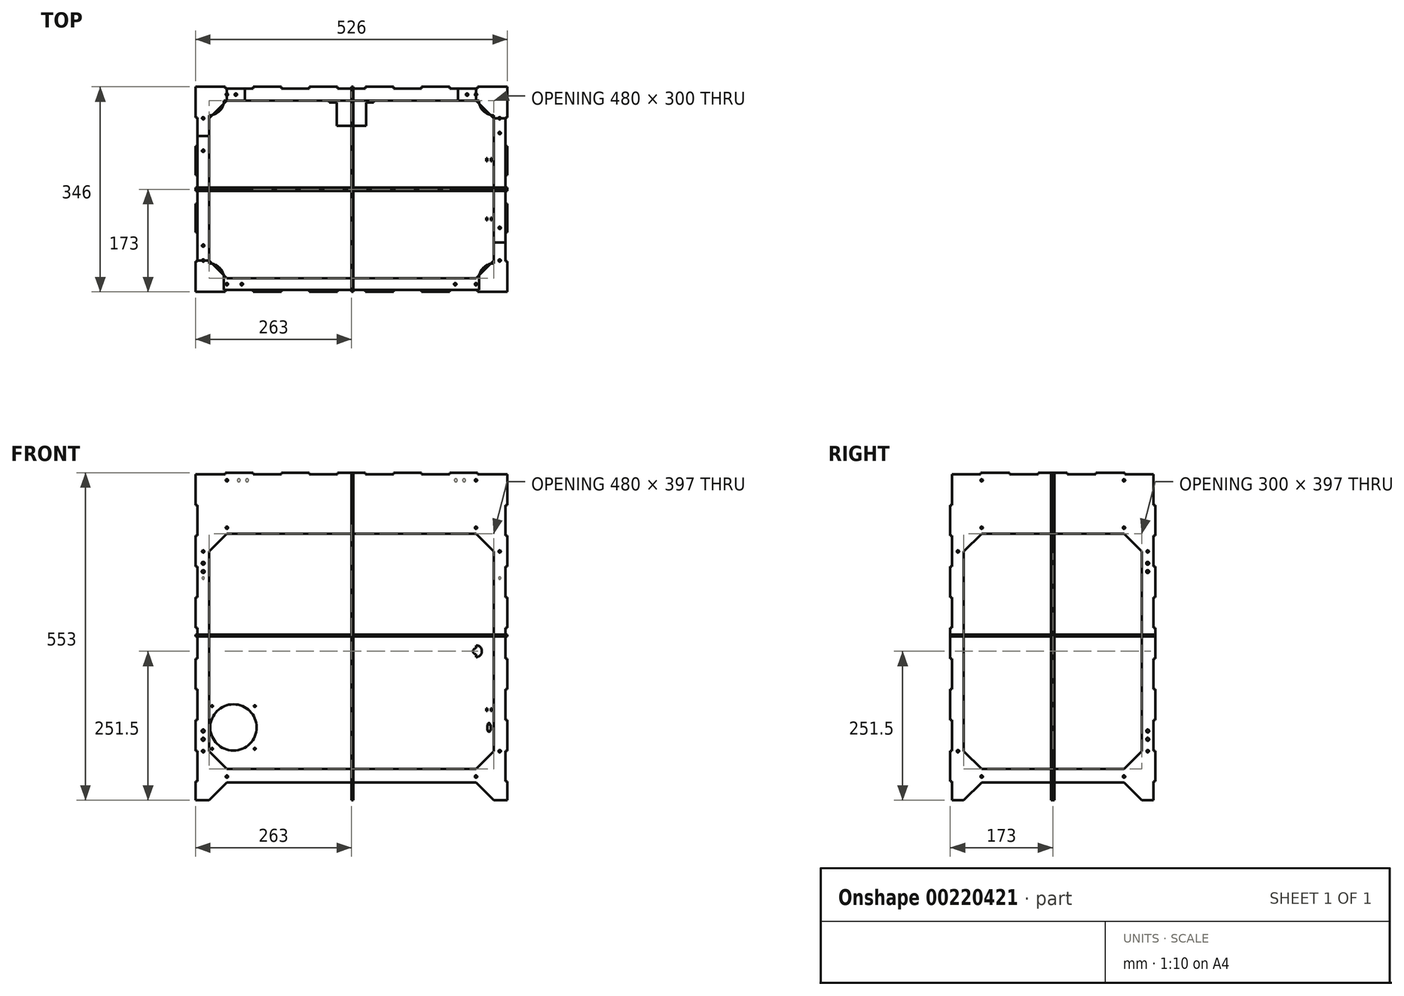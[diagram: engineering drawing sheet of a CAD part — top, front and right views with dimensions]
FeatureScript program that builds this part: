
annotation { "Feature Type Name" : "Feature", "Feature Type Description" : "" }
export const myFeature = defineFeature(function(context is Context, id is Id, definition is map)
    precondition{}
    {
        {
            assignVariable(context, id + "F0", {"name" : "thick", "anyValue" : 3});
        }
        {
            var Q0;
            Q0=qCreatedBy(makeId("Top.planeOp"),FACE);
            var sketch = newSketch(context, id + "F1", { "sketchPlane" : qUnion([Q0])});
            skLineSegment(sketch, "E0.bottom", {"start": v(263, -173) * mm, "end": v(-263, -173) * mm});
            skLineSegment(sketch, "E0.top", {"start": v(263, 173) * mm, "end": v(-263, 173) * mm});
            skLineSegment(sketch, "E0.left", {"start": v(263, -173) * mm, "end": v(263, 173) * mm});
            skLineSegment(sketch, "E0.right", {"start": v(-263, -173) * mm, "end": v(-263, 173) * mm});
            skPoint(sketch, "E0.middle", {"position": v(0, 0) * mm});
            skLineSegment(sketch, "E1.bottom", {"start": v(210, -150) * mm, "end": v(-210, -150) * mm});
            skLineSegment(sketch, "E1.top", {"start": v(210, 150) * mm, "end": v(-210, 150) * mm});
            skLineSegment(sketch, "E1.left", {"start": v(240, -120) * mm, "end": v(240, 120) * mm});
            skLineSegment(sketch, "E1.right", {"start": v(-240, -120) * mm, "end": v(-240, 120) * mm});
            skLineSegment(sketch, "E2", {"start": v(-210, 150) * mm, "end": v(-240, 120) * mm});
            skLineSegment(sketch, "E3", {"start": v(-240, -120) * mm, "end": v(-210, -150) * mm});
            skLineSegment(sketch, "E4", {"start": v(240, -120) * mm, "end": v(210, -150) * mm});
            skLineSegment(sketch, "E5", {"start": v(240, 120) * mm, "end": v(210, 150) * mm});
            skPoint(sketch, "E6.orphan", {"position": v(-240, 150) * mm});
            skPoint(sketch, "E7.orphan", {"position": v(-240, -150) * mm});
            skPoint(sketch, "E8.orphan", {"position": v(240, -150) * mm});
            skPoint(sketch, "E9.orphan", {"position": v(240, 150) * mm});
            skCircle(sketch, "E10", {"center": v(-210, 160) * mm, "radius": 2 * mm});
            skCircle(sketch, "E11", {"center": v(210, 160) * mm, "radius": 2 * mm});
            skCircle(sketch, "E12", {"center": v(-250, 120) * mm, "radius": 2 * mm});
            skCircle(sketch, "E13", {"center": v(-250, -120) * mm, "radius": 2 * mm});
            skCircle(sketch, "E14", {"center": v(-210, -160) * mm, "radius": 2 * mm});
            skCircle(sketch, "E15", {"center": v(210, -160) * mm, "radius": 2 * mm});
            skCircle(sketch, "E16", {"center": v(250, -120) * mm, "radius": 2 * mm});
            skCircle(sketch, "E17", {"center": v(250, 120) * mm, "radius": 2 * mm});
            skLineSegment(sketch, "E18", {"start": v(-212.73, -173) * mm, "end": v(-212.73, -170) * mm});
            skLineSegment(sketch, "E19", {"start": v(-212.73, -170) * mm, "end": v(-165.45, -170) * mm});
            skLineSegment(sketch, "E20", {"start": v(-165.45, -170) * mm, "end": v(-165.45, -173) * mm});
            skLineSegment(sketch, "E21.1.0.0", {"start": v(-118.18, -173) * mm, "end": v(-118.18, -170) * mm});
            skLineSegment(sketch, "E21.1.0.1", {"start": v(-118.18, -170) * mm, "end": v(-70.9, -170) * mm});
            skLineSegment(sketch, "E21.1.0.2", {"start": v(-70.9, -170) * mm, "end": v(-70.9, -173) * mm});
            skLineSegment(sketch, "E21.2.0.0", {"start": v(-23.64, -173) * mm, "end": v(-23.64, -170) * mm});
            skLineSegment(sketch, "E21.2.0.1", {"start": v(-23.64, -170) * mm, "end": v(23.64, -170) * mm});
            skLineSegment(sketch, "E21.2.0.2", {"start": v(23.64, -170) * mm, "end": v(23.64, -173) * mm});
            skLineSegment(sketch, "E21.3.0.0", {"start": v(70.9, -173) * mm, "end": v(70.9, -170) * mm});
            skLineSegment(sketch, "E21.3.0.1", {"start": v(70.9, -170) * mm, "end": v(118.18, -170) * mm});
            skLineSegment(sketch, "E21.3.0.2", {"start": v(118.18, -170) * mm, "end": v(118.18, -173) * mm});
            skLineSegment(sketch, "E21.direction1", {"start": v(-212.73, -173) * mm, "end": v(-118.18, -173) * mm, "construction": true});
            skLineSegment(sketch, "E22", {"start": v(-212.73, 173) * mm, "end": v(-212.73, 170) * mm});
            skLineSegment(sketch, "E23", {"start": v(-212.73, 170) * mm, "end": v(-165.45, 170) * mm});
            skLineSegment(sketch, "E24", {"start": v(-165.45, 170) * mm, "end": v(-165.45, 173) * mm});
            skLineSegment(sketch, "E25.1.0.0", {"start": v(-118.18, 173) * mm, "end": v(-118.18, 170) * mm});
            skLineSegment(sketch, "E25.1.0.1", {"start": v(-118.18, 170) * mm, "end": v(-70.9, 170) * mm});
            skLineSegment(sketch, "E25.1.0.2", {"start": v(-70.9, 170) * mm, "end": v(-70.9, 173) * mm});
            skLineSegment(sketch, "E25.2.0.0", {"start": v(-23.64, 173) * mm, "end": v(-23.64, 170) * mm});
            skLineSegment(sketch, "E25.2.0.1", {"start": v(-23.64, 170) * mm, "end": v(23.64, 170) * mm});
            skLineSegment(sketch, "E25.2.0.2", {"start": v(23.64, 170) * mm, "end": v(23.64, 173) * mm});
            skLineSegment(sketch, "E25.3.0.0", {"start": v(70.9, 173) * mm, "end": v(70.9, 170) * mm});
            skLineSegment(sketch, "E25.3.0.1", {"start": v(70.9, 170) * mm, "end": v(118.18, 170) * mm});
            skLineSegment(sketch, "E25.3.0.2", {"start": v(118.18, 170) * mm, "end": v(118.18, 173) * mm});
            skLineSegment(sketch, "E25.direction1", {"start": v(-212.73, 170) * mm, "end": v(-118.18, 170) * mm, "construction": true});
            skLineSegment(sketch, "E26", {"start": v(-263, -72.86) * mm, "end": v(-260, -72.86) * mm});
            skLineSegment(sketch, "E27", {"start": v(-260, -72.86) * mm, "end": v(-260, -121.43) * mm});
            skLineSegment(sketch, "E28", {"start": v(-260, -121.43) * mm, "end": v(-263, -121.43) * mm});
            skLineSegment(sketch, "E29.0.1.0", {"start": v(-263, 24.29) * mm, "end": v(-260, 24.29) * mm});
            skLineSegment(sketch, "E29.0.1.1", {"start": v(-260, 24.29) * mm, "end": v(-260, -24.29) * mm});
            skLineSegment(sketch, "E29.0.1.2", {"start": v(-260, -24.29) * mm, "end": v(-263, -24.29) * mm});
            skLineSegment(sketch, "E29.0.2.0", {"start": v(-263, 121.43) * mm, "end": v(-260, 121.43) * mm});
            skLineSegment(sketch, "E29.0.2.1", {"start": v(-260, 121.43) * mm, "end": v(-260, 72.86) * mm});
            skLineSegment(sketch, "E29.0.2.2", {"start": v(-260, 72.86) * mm, "end": v(-263, 72.86) * mm});
            skLineSegment(sketch, "E29.direction1", {"start": v(-263, -72.86) * mm, "end": v(-188, -72.86) * mm, "construction": true});
            skLineSegment(sketch, "E29.direction2", {"start": v(-263, -72.86) * mm, "end": v(-263, 24.29) * mm, "construction": true});
            skLineSegment(sketch, "E30", {"start": v(263, -121.43) * mm, "end": v(260, -121.43) * mm});
            skLineSegment(sketch, "E31", {"start": v(260, -121.43) * mm, "end": v(260, -72.86) * mm});
            skLineSegment(sketch, "E32", {"start": v(260, -72.86) * mm, "end": v(263, -72.86) * mm});
            skLineSegment(sketch, "E33.0.1.0", {"start": v(260, 24.29) * mm, "end": v(263, 24.29) * mm});
            skLineSegment(sketch, "E33.0.1.1", {"start": v(260, -24.29) * mm, "end": v(260, 24.29) * mm});
            skLineSegment(sketch, "E33.0.1.2", {"start": v(263, -24.29) * mm, "end": v(260, -24.29) * mm});
            skLineSegment(sketch, "E33.0.2.0", {"start": v(260, 121.43) * mm, "end": v(263, 121.43) * mm});
            skLineSegment(sketch, "E33.0.2.1", {"start": v(260, 72.86) * mm, "end": v(260, 121.43) * mm});
            skLineSegment(sketch, "E33.0.2.2", {"start": v(263, 72.86) * mm, "end": v(260, 72.86) * mm});
            skLineSegment(sketch, "E33.direction1", {"start": v(235, -72.86) * mm, "end": v(260, -72.86) * mm, "construction": true});
            skLineSegment(sketch, "E33.direction2", {"start": v(260, -72.86) * mm, "end": v(260, 24.29) * mm, "construction": true});
            skCircle(sketch, "E34", {"center": v(-190, 160) * mm, "radius": 2 * mm, "construction": true});
            skCircle(sketch, "E35", {"center": v(-176, 160) * mm, "radius": 2 * mm, "construction": true});
            skCircle(sketch, "E36", {"center": v(190, 160) * mm, "radius": 2 * mm, "construction": true});
            skCircle(sketch, "E37", {"center": v(176, 160) * mm, "radius": 2 * mm, "construction": true});
            skPoint(sketch, "E38.centerSnap0", {"position": v(-260, 97.14) * mm});
            skLineSegment(sketch, "E39.0.4.0", {"start": v(165.45, -173) * mm, "end": v(165.45, -170) * mm});
            skLineSegment(sketch, "E39.3.4.0", {"start": v(165.45, -170) * mm, "end": v(212.73, -170) * mm});
            skLineSegment(sketch, "E39.6.4.0", {"start": v(212.73, -170) * mm, "end": v(212.73, -173) * mm});
            skLineSegment(sketch, "E40.0.4.0", {"start": v(165.45, 173) * mm, "end": v(165.45, 170) * mm});
            skLineSegment(sketch, "E40.3.4.0", {"start": v(165.45, 170) * mm, "end": v(212.73, 170) * mm});
            skLineSegment(sketch, "E40.6.4.0", {"start": v(212.73, 170) * mm, "end": v(212.73, 173) * mm});
            skSolve(sketch);
        }
        {
            var Q0;
            Q0=makeQuery(id+"F1.imprint","IMPRINT",FACE,{"disambiguationData":[TD([[makeQuery(id+"F1.imprint","IMPRINT",EDGE,{"derivedFrom":sQuery(id+"F1.wireOp",EDGE,"E0.bottom")}),-1.0]])]});
            extrude(context, id + "F2", {"entities" : qUnion([Q0]), "depth" : (getVariable(context, 'thick')) * mm});
        }
        {
            var Q0;
            Q0=qCreatedBy(makeId("Front.planeOp"),FACE);
            var sketch = newSketch(context, id + "F3", { "sketchPlane" : qUnion([Q0])});
            skLineSegment(sketch, "E41.bottom", {"start": v(263, -276.5) * mm, "end": v(240, -276.5) * mm});
            skLineSegment(sketch, "E41.top", {"start": v(263, 276.5) * mm, "end": v(-263, 276.5) * mm});
            skLineSegment(sketch, "E41.left", {"start": v(263, -276.5) * mm, "end": v(263, 276.5) * mm});
            skLineSegment(sketch, "E41.right", {"start": v(-263, -276.5) * mm, "end": v(-263, 276.5) * mm});
            skPoint(sketch, "E41.middle", {"position": v(0, 0) * mm});
            skLineSegment(sketch, "E42.bottom", {"start": v(210, 173.5) * mm, "end": v(-210, 173.5) * mm});
            skLineSegment(sketch, "E42.top", {"start": v(210, -223.5) * mm, "end": v(-210, -223.5) * mm});
            skLineSegment(sketch, "E42.left", {"start": v(240, 143.5) * mm, "end": v(240, -193.5) * mm});
            skLineSegment(sketch, "E42.right", {"start": v(-240, 143.5) * mm, "end": v(-240, -193.5) * mm});
            skPoint(sketch, "E42.middle", {"position": v(0, -25) * mm});
            skLineSegment(sketch, "E43", {"start": v(-210, 173.5) * mm, "end": v(-240, 143.5) * mm});
            skLineSegment(sketch, "E44", {"start": v(-240, -193.5) * mm, "end": v(-210, -223.5) * mm});
            skLineSegment(sketch, "E45", {"start": v(240, -193.5) * mm, "end": v(210, -223.5) * mm});
            skLineSegment(sketch, "E46", {"start": v(210, 173.5) * mm, "end": v(240, 143.5) * mm});
            skPoint(sketch, "E47.orphan", {"position": v(-240, 173.5) * mm});
            skPoint(sketch, "E48.orphan", {"position": v(-240, -223.5) * mm});
            skPoint(sketch, "E49.orphan", {"position": v(240, 173.5) * mm});
            skPoint(sketch, "E50.orphan", {"position": v(240, -223.5) * mm});
            skLineSegment(sketch, "E51", {"start": v(-240, -276.5) * mm, "end": v(-210, -246.5) * mm});
            skLineSegment(sketch, "E52", {"start": v(-210, -246.5) * mm, "end": v(210, -246.5) * mm});
            skLineSegment(sketch, "E53", {"start": v(210, -246.5) * mm, "end": v(240, -276.5) * mm});
            skLineSegment(sketch, "E54.trimOffspring", {"start": v(-240, -276.5) * mm, "end": v(-263, -276.5) * mm});
            skCircle(sketch, "E55", {"center": v(-210, 263.5) * mm, "radius": 2 * mm});
            skCircle(sketch, "E56", {"center": v(210, 263.5) * mm, "radius": 2 * mm});
            skCircle(sketch, "E57", {"center": v(-210, 183.5) * mm, "radius": 2 * mm});
            skCircle(sketch, "E58", {"center": v(210, 183.5) * mm, "radius": 2 * mm});
            skCircle(sketch, "E59", {"center": v(250, 143.5) * mm, "radius": 2 * mm});
            skCircle(sketch, "E60", {"center": v(-250, 143.5) * mm, "radius": 2 * mm});
            skCircle(sketch, "E61", {"center": v(250, -193.5) * mm, "radius": 2 * mm});
            skCircle(sketch, "E62", {"center": v(210, -236.5) * mm, "radius": 2 * mm});
            skCircle(sketch, "E63", {"center": v(-210, -236.5) * mm, "radius": 2 * mm});
            skCircle(sketch, "E64", {"center": v(-250, -193.5) * mm, "radius": 2 * mm});
            skCircle(sketch, "E65", {"center": v(-250, 123.5) * mm, "radius": 2.5 * mm});
            skCircle(sketch, "E66", {"center": v(-250, 109.5) * mm, "radius": 2.5 * mm});
            skCircle(sketch, "E67", {"center": v(-250, -173.5) * mm, "radius": 2.5 * mm});
            skCircle(sketch, "E68", {"center": v(-250, -159.5) * mm, "radius": 2.5 * mm});
            skLineSegment(sketch, "E69", {"start": v(-260, 276.5) * mm, "end": v(-260, 273.5) * mm});
            skLineSegment(sketch, "E70", {"start": v(-260, 273.5) * mm, "end": v(-212.73, 273.5) * mm});
            skLineSegment(sketch, "E71", {"start": v(-212.73, 273.5) * mm, "end": v(-212.73, 276.5) * mm});
            skLineSegment(sketch, "E72.1.0.0", {"start": v(-165.45, 276.5) * mm, "end": v(-165.45, 273.5) * mm});
            skLineSegment(sketch, "E72.1.0.1", {"start": v(-165.45, 273.5) * mm, "end": v(-118.18, 273.5) * mm});
            skLineSegment(sketch, "E72.1.0.2", {"start": v(-118.18, 273.5) * mm, "end": v(-118.18, 276.5) * mm});
            skLineSegment(sketch, "E72.2.0.0", {"start": v(-70.9, 276.5) * mm, "end": v(-70.9, 273.5) * mm});
            skLineSegment(sketch, "E72.2.0.1", {"start": v(-70.9, 273.5) * mm, "end": v(-23.64, 273.5) * mm});
            skLineSegment(sketch, "E72.2.0.2", {"start": v(-23.64, 273.5) * mm, "end": v(-23.64, 276.5) * mm});
            skLineSegment(sketch, "E72.3.0.0", {"start": v(23.64, 276.5) * mm, "end": v(23.64, 273.5) * mm});
            skLineSegment(sketch, "E72.3.0.1", {"start": v(23.64, 273.5) * mm, "end": v(70.9, 273.5) * mm});
            skLineSegment(sketch, "E72.3.0.2", {"start": v(70.9, 273.5) * mm, "end": v(70.9, 276.5) * mm});
            skLineSegment(sketch, "E72.4.0.0", {"start": v(118.18, 276.5) * mm, "end": v(118.18, 273.5) * mm});
            skLineSegment(sketch, "E72.4.0.1", {"start": v(118.18, 273.5) * mm, "end": v(165.45, 273.5) * mm});
            skLineSegment(sketch, "E72.4.0.2", {"start": v(165.45, 273.5) * mm, "end": v(165.45, 276.5) * mm});
            skLineSegment(sketch, "E72.direction1", {"start": v(-260, 273.5) * mm, "end": v(-165.45, 273.5) * mm, "construction": true});
            skLineSegment(sketch, "E73", {"start": v(-263, 273.5) * mm, "end": v(-260, 273.5) * mm});
            skLineSegment(sketch, "E74", {"start": v(263, 273.5) * mm, "end": v(260, 273.5) * mm});
            skLineSegment(sketch, "E75", {"start": v(-263, -192.86) * mm, "end": v(-260, -192.86) * mm});
            skLineSegment(sketch, "E76", {"start": v(-260, -192.86) * mm, "end": v(-260, -244.68) * mm});
            skLineSegment(sketch, "E77", {"start": v(-260, -244.68) * mm, "end": v(-263, -244.68) * mm});
            skLineSegment(sketch, "E78.0.1.0", {"start": v(-260, -89.23) * mm, "end": v(-260, -141.05) * mm});
            skLineSegment(sketch, "E78.0.1.1", {"start": v(-263, -89.23) * mm, "end": v(-260, -89.23) * mm});
            skLineSegment(sketch, "E78.0.1.2", {"start": v(-260, -141.05) * mm, "end": v(-263, -141.05) * mm});
            skLineSegment(sketch, "E78.0.2.0", {"start": v(-260, 14.4) * mm, "end": v(-260, -37.4) * mm});
            skLineSegment(sketch, "E78.0.2.1", {"start": v(-263, 14.4) * mm, "end": v(-260, 14.4) * mm});
            skLineSegment(sketch, "E78.0.2.2", {"start": v(-260, -37.4) * mm, "end": v(-263, -37.4) * mm});
            skLineSegment(sketch, "E78.0.3.0", {"start": v(-260, 118.05) * mm, "end": v(-260, 66.23) * mm});
            skLineSegment(sketch, "E78.0.3.1", {"start": v(-263, 118.05) * mm, "end": v(-260, 118.05) * mm});
            skLineSegment(sketch, "E78.0.3.2", {"start": v(-260, 66.23) * mm, "end": v(-263, 66.23) * mm});
            skLineSegment(sketch, "E78.direction1", {"start": v(-260, -244.68) * mm, "end": v(-185.37, -244.68) * mm, "construction": true});
            skLineSegment(sketch, "E78.direction2", {"start": v(-260, -244.68) * mm, "end": v(-260, -141.05) * mm, "construction": true});
            skLineSegment(sketch, "E79", {"start": v(263, -244.68) * mm, "end": v(260, -244.68) * mm});
            skLineSegment(sketch, "E80", {"start": v(260, -244.68) * mm, "end": v(260, -192.86) * mm});
            skLineSegment(sketch, "E81", {"start": v(260, -192.86) * mm, "end": v(263, -192.86) * mm});
            skLineSegment(sketch, "E82.0.1.0", {"start": v(260, -89.23) * mm, "end": v(263, -89.23) * mm});
            skLineSegment(sketch, "E82.0.1.1", {"start": v(260, -141.05) * mm, "end": v(260, -89.23) * mm});
            skLineSegment(sketch, "E82.0.1.2", {"start": v(263, -141.05) * mm, "end": v(260, -141.05) * mm});
            skLineSegment(sketch, "E82.0.2.0", {"start": v(260, 14.4) * mm, "end": v(263, 14.4) * mm});
            skLineSegment(sketch, "E82.0.2.1", {"start": v(260, -37.4) * mm, "end": v(260, 14.4) * mm});
            skLineSegment(sketch, "E82.0.2.2", {"start": v(263, -37.4) * mm, "end": v(260, -37.4) * mm});
            skLineSegment(sketch, "E82.0.3.0", {"start": v(260, 118.05) * mm, "end": v(263, 118.05) * mm});
            skLineSegment(sketch, "E82.0.3.1", {"start": v(260, 66.23) * mm, "end": v(260, 118.05) * mm});
            skLineSegment(sketch, "E82.0.3.2", {"start": v(263, 66.23) * mm, "end": v(260, 66.23) * mm});
            skLineSegment(sketch, "E82.direction1", {"start": v(260, -192.86) * mm, "end": v(285, -192.86) * mm, "construction": true});
            skLineSegment(sketch, "E82.direction2", {"start": v(260, -192.86) * mm, "end": v(260, -89.23) * mm, "construction": true});
            skCircle(sketch, "E83", {"center": v(190, 263.5) * mm, "radius": 2.5 * mm});
            skCircle(sketch, "E84", {"center": v(176, 263.5) * mm, "radius": 2.5 * mm});
            skCircle(sketch, "E85", {"center": v(-190, 263.5) * mm, "radius": 2.5 * mm});
            skCircle(sketch, "E86", {"center": v(-176, 263.5) * mm, "radius": 2.5 * mm});
            skCircle(sketch, "E87", {"center": v(250, 98.5) * mm, "radius": 2 * mm});
            skArc(sketch, "E88", {"start": v(210, -15) * mm, "mid": v(220, -25) * mm, "end": v(210, -35) * mm});
            skArc(sketch, "E89", {"start": v(210, -20) * mm, "mid": v(205, -25) * mm, "end": v(210, -30) * mm});
            skLineSegment(sketch, "E90", {"start": v(210, -20) * mm, "end": v(210, -15) * mm});
            skLineSegment(sketch, "E91", {"start": v(210, -30) * mm, "end": v(210, -35) * mm});
            skCircle(sketch, "E92", {"center": v(-250, 98.5) * mm, "radius": 2 * mm});
            skLineSegment(sketch, "E93.bottom", {"start": v(-159, -113.5) * mm, "end": v(-239, -113.5) * mm, "construction": true});
            skLineSegment(sketch, "E93.top", {"start": v(-159, -193.5) * mm, "end": v(-239, -193.5) * mm, "construction": true});
            skLineSegment(sketch, "E93.left", {"start": v(-159, -113.5) * mm, "end": v(-159, -193.5) * mm, "construction": true});
            skLineSegment(sketch, "E93.right", {"start": v(-239, -113.5) * mm, "end": v(-239, -193.5) * mm, "construction": true});
            skPoint(sketch, "E93.middle", {"position": v(-199, -153.5) * mm});
            skCircle(sketch, "E94", {"center": v(-199, -153.5) * mm, "radius": 39 * mm});
            skLineSegment(sketch, "E95.bottom", {"start": v(-163, -117.5) * mm, "end": v(-235, -117.5) * mm, "construction": true});
            skLineSegment(sketch, "E95.top", {"start": v(-163, -189.5) * mm, "end": v(-235, -189.5) * mm, "construction": true});
            skLineSegment(sketch, "E95.left", {"start": v(-163, -117.5) * mm, "end": v(-163, -189.5) * mm, "construction": true});
            skLineSegment(sketch, "E95.right", {"start": v(-235, -117.5) * mm, "end": v(-235, -189.5) * mm, "construction": true});
            skCircle(sketch, "E96", {"center": v(-163, -117.5) * mm, "radius": 1.5 * mm});
            skCircle(sketch, "E97", {"center": v(-235, -117.5) * mm, "radius": 1.5 * mm});
            skCircle(sketch, "E98", {"center": v(-163, -189.5) * mm, "radius": 1.5 * mm});
            skCircle(sketch, "E99", {"center": v(-235, -189.5) * mm, "radius": 1.5 * mm});
            skEllipse(sketch, "E100", {"center": v(232, -153.5) * mm, "majorRadius": 7.5 * mm, "minorRadius": 3 * mm, "majorAxis": v(0, -1)});
            skLineSegment(sketch, "E101.bottom", {"start": v(227, -121.5) * mm, "end": v(229, -121.5) * mm});
            skLineSegment(sketch, "E101.top", {"start": v(227, -125.5) * mm, "end": v(229, -125.5) * mm});
            skLineSegment(sketch, "E101.left", {"start": v(227, -121.5) * mm, "end": v(227, -125.5) * mm});
            skLineSegment(sketch, "E101.right", {"start": v(229, -121.5) * mm, "end": v(229, -125.5) * mm});
            skLineSegment(sketch, "E102.bottom", {"start": v(235, -121.5) * mm, "end": v(237, -121.5) * mm});
            skLineSegment(sketch, "E102.top", {"start": v(235, -125.5) * mm, "end": v(237, -125.5) * mm});
            skLineSegment(sketch, "E102.left", {"start": v(235, -121.5) * mm, "end": v(235, -125.5) * mm});
            skLineSegment(sketch, "E102.right", {"start": v(237, -121.5) * mm, "end": v(237, -125.5) * mm});
            skPoint(sketch, "E103", {"position": v(232, -123.5) * mm});
            skPoint(sketch, "E104", {"position": v(229, -123.5) * mm});
            skPoint(sketch, "E105", {"position": v(235, -123.5) * mm});
            skLineSegment(sketch, "E106.0.0.4", {"start": v(-260, 221.68) * mm, "end": v(-260, 169.86) * mm});
            skLineSegment(sketch, "E106.3.0.4", {"start": v(-263, 221.68) * mm, "end": v(-260, 221.68) * mm});
            skLineSegment(sketch, "E106.6.0.4", {"start": v(-260, 169.86) * mm, "end": v(-263, 169.86) * mm});
            skLineSegment(sketch, "E107.0.0.4", {"start": v(260, 221.68) * mm, "end": v(263, 221.68) * mm});
            skLineSegment(sketch, "E107.3.0.4", {"start": v(260, 169.86) * mm, "end": v(260, 221.68) * mm});
            skLineSegment(sketch, "E107.6.0.4", {"start": v(263, 169.86) * mm, "end": v(260, 169.86) * mm});
            skLineSegment(sketch, "E108.0.5.0", {"start": v(212.73, 276.5) * mm, "end": v(212.73, 273.5) * mm});
            skLineSegment(sketch, "E108.3.5.0", {"start": v(212.73, 273.5) * mm, "end": v(260, 273.5) * mm});
            skLineSegment(sketch, "E108.6.5.0", {"start": v(260, 273.5) * mm, "end": v(260, 276.5) * mm});
            skCircle(sketch, "E109", {"center": v(-230, 123.5) * mm, "radius": 2.5 * mm});
            skCircle(sketch, "E110", {"center": v(-230, 109.5) * mm, "radius": 2.5 * mm});
            skCircle(sketch, "E111", {"center": v(-230, -159.5) * mm, "radius": 2.5 * mm});
            skCircle(sketch, "E112", {"center": v(-230, -173.5) * mm, "radius": 2.5 * mm});
            skSolve(sketch);
        }
        {
            var Q0;
            Q0=makeQuery(id+"F3.imprint","IMPRINT",FACE,{"disambiguationData":[TD([[makeQuery(id+"F3.imprint","IMPRINT",EDGE,{"derivedFrom":sQuery(id+"F3.wireOp",EDGE,"E41.bottom")}),-1.0]])]});
            var Q1;
            Q1=makeQuery(id+"F3.imprint","IMPRINT",FACE,{"disambiguationData":[TD([[makeQuery(id+"F3.imprint","IMPRINT",EDGE,{"derivedFrom":sQuery(id+"F3.wireOp",EDGE,"E85")}),1.0]])]});
            var Q2;
            Q2=makeQuery(id+"F3.imprint","IMPRINT",FACE,{"disambiguationData":[TD([[makeQuery(id+"F3.imprint","IMPRINT",EDGE,{"derivedFrom":sQuery(id+"F3.wireOp",EDGE,"E86")}),1.0]])]});
            var Q3;
            Q3=makeQuery(id+"F3.imprint","IMPRINT",FACE,{"disambiguationData":[TD([[makeQuery(id+"F3.imprint","IMPRINT",EDGE,{"derivedFrom":sQuery(id+"F3.wireOp",EDGE,"E84")}),1.0]])]});
            var Q4;
            Q4=makeQuery(id+"F3.imprint","IMPRINT",FACE,{"disambiguationData":[TD([[makeQuery(id+"F3.imprint","IMPRINT",EDGE,{"derivedFrom":sQuery(id+"F3.wireOp",EDGE,"E83")}),1.0]])]});
            var Q5;
            Q5=makeQuery(id+"F3.imprint","IMPRINT",FACE,{"disambiguationData":[TD([[makeQuery(id+"F3.imprint","IMPRINT",EDGE,{"derivedFrom":sQuery(id+"F3.wireOp",EDGE,"E92")}),1.0]])]});
            var Q6;
            Q6=makeQuery(id+"F3.imprint","IMPRINT",FACE,{"disambiguationData":[TD([[makeQuery(id+"F3.imprint","IMPRINT",EDGE,{"derivedFrom":sQuery(id+"F3.wireOp",EDGE,"E87")}),1.0]])]});
            extrude(context, id + "F4", {"entities" : qUnion([Q0, Q1, Q2, Q3, Q4, Q5, Q6]), "depth" : (getVariable(context, 'thick')) * mm});
        }
        {
            var Q0;
            Q0=makeQuery(id+"F3.imprint","IMPRINT",FACE,{"disambiguationData":[TD([[makeQuery(id+"F3.imprint","IMPRINT",EDGE,{"derivedFrom":sQuery(id+"F3.wireOp",EDGE,"E41.bottom")}),-1.0]])]});
            var Q1;
            Q1=makeQuery(id+"F3.imprint","IMPRINT",FACE,{"disambiguationData":[TD([[makeQuery(id+"F3.imprint","IMPRINT",EDGE,{"derivedFrom":sQuery(id+"F3.wireOp",EDGE,"E42.bottom")}),1.0]])]});
            var Q2;
            Q2=makeQuery(id+"F3.imprint","IMPRINT",FACE,{"disambiguationData":[TD([[makeQuery(id+"F3.imprint","IMPRINT",EDGE,{"derivedFrom":sQuery(id+"F3.wireOp",EDGE,"E65")}),1.0]])]});
            var Q3;
            Q3=makeQuery(id+"F3.imprint","IMPRINT",FACE,{"disambiguationData":[TD([[makeQuery(id+"F3.imprint","IMPRINT",EDGE,{"derivedFrom":sQuery(id+"F3.wireOp",EDGE,"E68")}),1.0]])]});
            var Q4;
            Q4=makeQuery(id+"F3.imprint","IMPRINT",FACE,{"disambiguationData":[TD([[makeQuery(id+"F3.imprint","IMPRINT",EDGE,{"derivedFrom":sQuery(id+"F3.wireOp",EDGE,"E67")}),1.0]])]});
            var Q5;
            Q5=makeQuery(id+"F3.imprint","IMPRINT",FACE,{"disambiguationData":[TD([[makeQuery(id+"F3.imprint","IMPRINT",EDGE,{"derivedFrom":sQuery(id+"F3.wireOp",EDGE,"E88")}),-1.0]])]});
            var Q6;
            Q6=makeQuery(id+"F3.imprint","IMPRINT",FACE,{"disambiguationData":[TD([[makeQuery(id+"F3.imprint","IMPRINT",EDGE,{"derivedFrom":sQuery(id+"F3.wireOp",EDGE,"E66")}),1.0]])]});
            var Q7;
            {var subQ0=sQuery(id+"F3.wireOp",EDGE,"E112");var subQ1=sQuery(id+"F3.wireOp",EDGE,"E94");var subQ2=makeQuery(id+"F3.imprint","INTERSECT",VERTEX,{"disambiguationData":[OD(0.0)],"derivedFrom":[subQ1,subQ0]});Q7=makeQuery(id+"F3.imprint","IMPRINT",FACE,{"disambiguationData":[TD([[makeQuery(id+"F3.imprint","IMPRINT",EDGE,{"disambiguationData":[TD([[subQ2,-1.0]])],"derivedFrom":subQ1}),-1.0]])]});}
            var Q8;
            Q8=makeQuery(id+"F3.imprint","IMPRINT",FACE,{"disambiguationData":[TD([[makeQuery(id+"F3.imprint","IMPRINT",EDGE,{"derivedFrom":sQuery(id+"F3.wireOp",EDGE,"E109")}),1.0]])]});
            var Q9;
            Q9=makeQuery(id+"F3.imprint","IMPRINT",FACE,{"disambiguationData":[TD([[makeQuery(id+"F3.imprint","IMPRINT",EDGE,{"derivedFrom":sQuery(id+"F3.wireOp",EDGE,"E110")}),1.0]])]});
            extrude(context, id + "F5", {"entities" : qUnion([Q0, Q1, Q2, Q3, Q4, Q5, Q6, Q7, Q8, Q9]), "oppositeDirection" : true, "depth" : (getVariable(context, 'thick')) * mm});
        }
        {
            var Q0;
            Q0=qCreatedBy(makeId("Right.planeOp"),FACE);
            var sketch = newSketch(context, id + "F6", { "sketchPlane" : qUnion([Q0])});
            skLineSegment(sketch, "E113.bottom", {"start": v(-173, -276.5) * mm, "end": v(173, -276.5) * mm});
            skLineSegment(sketch, "E113.top", {"start": v(-173, 276.5) * mm, "end": v(173, 276.5) * mm});
            skLineSegment(sketch, "E113.left", {"start": v(-173, -276.5) * mm, "end": v(-173, 276.5) * mm});
            skLineSegment(sketch, "E113.right", {"start": v(173, -276.5) * mm, "end": v(173, 276.5) * mm});
            skPoint(sketch, "E113.middle", {"position": v(0, 0) * mm});
            skLineSegment(sketch, "E114.bottom", {"start": v(-120, 173.5) * mm, "end": v(120, 173.5) * mm});
            skLineSegment(sketch, "E114.top", {"start": v(-120, -223.5) * mm, "end": v(120, -223.5) * mm});
            skLineSegment(sketch, "E114.left", {"start": v(-150, 143.5) * mm, "end": v(-150, -193.5) * mm});
            skLineSegment(sketch, "E114.right", {"start": v(150, 143.5) * mm, "end": v(150, -193.5) * mm});
            skPoint(sketch, "E114.middle", {"position": v(0, -25) * mm});
            skLineSegment(sketch, "E115", {"start": v(120, 173.5) * mm, "end": v(150, 143.5) * mm});
            skLineSegment(sketch, "E116", {"start": v(-120, 173.5) * mm, "end": v(-150, 143.5) * mm});
            skLineSegment(sketch, "E117", {"start": v(-150, -193.5) * mm, "end": v(-120, -223.5) * mm});
            skLineSegment(sketch, "E118", {"start": v(120, -223.5) * mm, "end": v(150, -193.5) * mm});
            skPoint(sketch, "E119.orphan", {"position": v(150, 173.5) * mm});
            skPoint(sketch, "E120.orphan", {"position": v(-150, 173.5) * mm});
            skPoint(sketch, "E121.orphan", {"position": v(-150, -223.5) * mm});
            skPoint(sketch, "E122.orphan", {"position": v(150, -223.5) * mm});
            skLineSegment(sketch, "E123", {"start": v(150, -276.5) * mm, "end": v(120, -246.5) * mm});
            skLineSegment(sketch, "E124", {"start": v(120, -246.5) * mm, "end": v(-120, -246.5) * mm});
            skLineSegment(sketch, "E125", {"start": v(-120, -246.5) * mm, "end": v(-150, -276.5) * mm});
            skCircle(sketch, "E126", {"center": v(120, 183.5) * mm, "radius": 2 * mm});
            skCircle(sketch, "E127", {"center": v(-120, 183.5) * mm, "radius": 2 * mm});
            skCircle(sketch, "E128", {"center": v(-120, 263.5) * mm, "radius": 2 * mm});
            skCircle(sketch, "E129", {"center": v(120, 263.5) * mm, "radius": 2 * mm});
            skCircle(sketch, "E130", {"center": v(160, 143.5) * mm, "radius": 2 * mm});
            skCircle(sketch, "E131", {"center": v(160, -193.5) * mm, "radius": 2 * mm});
            skCircle(sketch, "E132", {"center": v(-160, 143.5) * mm, "radius": 2 * mm});
            skCircle(sketch, "E133", {"center": v(-160, -193.5) * mm, "radius": 2 * mm});
            skCircle(sketch, "E134", {"center": v(120, -236.5) * mm, "radius": 2 * mm});
            skCircle(sketch, "E135", {"center": v(-120, -236.5) * mm, "radius": 2 * mm});
            skCircle(sketch, "E136", {"center": v(160, 123.5) * mm, "radius": 2.5 * mm});
            skCircle(sketch, "E137", {"center": v(160, 109.5) * mm, "radius": 2.5 * mm});
            skCircle(sketch, "E138", {"center": v(160, -173.5) * mm, "radius": 2.5 * mm});
            skCircle(sketch, "E139", {"center": v(160, -159.5) * mm, "radius": 2.5 * mm});
            skLineSegment(sketch, "E140", {"start": v(-170, 276.5) * mm, "end": v(-170, 273.5) * mm});
            skLineSegment(sketch, "E141", {"start": v(170, 276.5) * mm, "end": v(170, 273.5) * mm});
            skLineSegment(sketch, "E142", {"start": v(173, -296.5) * mm, "end": v(170, -296.5) * mm});
            skLineSegment(sketch, "E143", {"start": v(170, -296.5) * mm, "end": v(170, -244.68) * mm});
            skLineSegment(sketch, "E144", {"start": v(170, -244.68) * mm, "end": v(173, -244.68) * mm});
            skLineSegment(sketch, "E145", {"start": v(-173, -296.5) * mm, "end": v(-170, -296.5) * mm});
            skLineSegment(sketch, "E146", {"start": v(-170, -296.5) * mm, "end": v(-170, -244.68) * mm});
            skLineSegment(sketch, "E147", {"start": v(-170, -244.68) * mm, "end": v(-173, -244.68) * mm});
            skLineSegment(sketch, "E148.0.1.0", {"start": v(173, -192.86) * mm, "end": v(170, -192.86) * mm});
            skLineSegment(sketch, "E148.0.1.1", {"start": v(170, -192.86) * mm, "end": v(170, -141.05) * mm});
            skLineSegment(sketch, "E148.0.1.2", {"start": v(170, -141.05) * mm, "end": v(173, -141.05) * mm});
            skLineSegment(sketch, "E148.0.1.3", {"start": v(-170, -141.05) * mm, "end": v(-173, -141.05) * mm});
            skLineSegment(sketch, "E148.0.1.4", {"start": v(-170, -192.86) * mm, "end": v(-170, -141.05) * mm});
            skLineSegment(sketch, "E148.0.1.5", {"start": v(-173, -192.86) * mm, "end": v(-170, -192.86) * mm});
            skLineSegment(sketch, "E148.0.2.0", {"start": v(173, -89.23) * mm, "end": v(170, -89.23) * mm});
            skLineSegment(sketch, "E148.0.2.1", {"start": v(170, -89.23) * mm, "end": v(170, -37.4) * mm});
            skLineSegment(sketch, "E148.0.2.2", {"start": v(170, -37.4) * mm, "end": v(173, -37.4) * mm});
            skLineSegment(sketch, "E148.0.2.3", {"start": v(-170, -37.4) * mm, "end": v(-173, -37.4) * mm});
            skLineSegment(sketch, "E148.0.2.4", {"start": v(-170, -89.23) * mm, "end": v(-170, -37.4) * mm});
            skLineSegment(sketch, "E148.0.2.5", {"start": v(-173, -89.23) * mm, "end": v(-170, -89.23) * mm});
            skLineSegment(sketch, "E148.0.3.0", {"start": v(173, 14.4) * mm, "end": v(170, 14.4) * mm});
            skLineSegment(sketch, "E148.0.3.1", {"start": v(170, 14.4) * mm, "end": v(170, 66.23) * mm});
            skLineSegment(sketch, "E148.0.3.2", {"start": v(170, 66.23) * mm, "end": v(173, 66.23) * mm});
            skLineSegment(sketch, "E148.0.3.3", {"start": v(-170, 66.23) * mm, "end": v(-173, 66.23) * mm});
            skLineSegment(sketch, "E148.0.3.4", {"start": v(-170, 14.4) * mm, "end": v(-170, 66.23) * mm});
            skLineSegment(sketch, "E148.0.3.5", {"start": v(-173, 14.4) * mm, "end": v(-170, 14.4) * mm});
            skLineSegment(sketch, "E148.0.4.0", {"start": v(173, 118.05) * mm, "end": v(170, 118.05) * mm});
            skLineSegment(sketch, "E148.0.4.1", {"start": v(170, 118.05) * mm, "end": v(170, 169.86) * mm});
            skLineSegment(sketch, "E148.0.4.2", {"start": v(170, 169.86) * mm, "end": v(173, 169.86) * mm});
            skLineSegment(sketch, "E148.0.4.3", {"start": v(-170, 169.86) * mm, "end": v(-173, 169.86) * mm});
            skLineSegment(sketch, "E148.0.4.4", {"start": v(-170, 118.05) * mm, "end": v(-170, 169.86) * mm});
            skLineSegment(sketch, "E148.0.4.5", {"start": v(-173, 118.05) * mm, "end": v(-170, 118.05) * mm});
            skLineSegment(sketch, "E148.direction1", {"start": v(170, -296.5) * mm, "end": v(186.73, -296.5) * mm, "construction": true});
            skLineSegment(sketch, "E148.direction2", {"start": v(170, -296.5) * mm, "end": v(170, -192.86) * mm, "construction": true});
            skLineSegment(sketch, "E149", {"start": v(-121.43, 276.5) * mm, "end": v(-121.43, 273.5) * mm});
            skLineSegment(sketch, "E150", {"start": v(-121.43, 273.5) * mm, "end": v(-170, 273.5) * mm});
            skLineSegment(sketch, "E151", {"start": v(-170, 273.5) * mm, "end": v(-170, 276.5) * mm});
            skLineSegment(sketch, "E152.1.0.0", {"start": v(-24.29, 276.5) * mm, "end": v(-24.29, 273.5) * mm});
            skLineSegment(sketch, "E152.1.0.1", {"start": v(-24.29, 273.5) * mm, "end": v(-72.86, 273.5) * mm});
            skLineSegment(sketch, "E152.1.0.2", {"start": v(-72.86, 273.5) * mm, "end": v(-72.86, 276.5) * mm});
            skLineSegment(sketch, "E152.2.0.0", {"start": v(72.86, 276.5) * mm, "end": v(72.86, 273.5) * mm});
            skLineSegment(sketch, "E152.2.0.1", {"start": v(72.86, 273.5) * mm, "end": v(24.29, 273.5) * mm});
            skLineSegment(sketch, "E152.2.0.2", {"start": v(24.29, 273.5) * mm, "end": v(24.29, 276.5) * mm});
            skLineSegment(sketch, "E152.direction1", {"start": v(-121.43, 273.5) * mm, "end": v(-24.29, 273.5) * mm, "construction": true});
            skArc(sketch, "E153", {"start": v(-120, -15) * mm, "mid": v(-130, -25) * mm, "end": v(-120, -35) * mm});
            skArc(sketch, "E154", {"start": v(-120, -20) * mm, "mid": v(-115, -25) * mm, "end": v(-120, -30) * mm});
            skLineSegment(sketch, "E155", {"start": v(-120, -20) * mm, "end": v(-120, -15) * mm});
            skLineSegment(sketch, "E156", {"start": v(-120, -30) * mm, "end": v(-120, -35) * mm});
            skLineSegment(sketch, "E157.0.0.5", {"start": v(173, 221.68) * mm, "end": v(170, 221.68) * mm});
            skLineSegment(sketch, "E157.3.0.5", {"start": v(170, 221.68) * mm, "end": v(170, 273.5) * mm});
            skLineSegment(sketch, "E157.6.0.5", {"start": v(170, 273.5) * mm, "end": v(173, 273.5) * mm});
            skLineSegment(sketch, "E157.9.0.5", {"start": v(-170, 273.5) * mm, "end": v(-173, 273.5) * mm});
            skLineSegment(sketch, "E157.12.0.5", {"start": v(-170, 221.68) * mm, "end": v(-170, 273.5) * mm});
            skLineSegment(sketch, "E157.15.0.5", {"start": v(-173, 221.68) * mm, "end": v(-170, 221.68) * mm});
            skLineSegment(sketch, "E158.3.3.0", {"start": v(170, 273.5) * mm, "end": v(121.43, 273.5) * mm});
            skLineSegment(sketch, "E158.6.3.0", {"start": v(121.43, 273.5) * mm, "end": v(121.43, 276.5) * mm});
            skCircle(sketch, "E159", {"center": v(140, -159.5) * mm, "radius": 2.5 * mm});
            skCircle(sketch, "E160", {"center": v(140, -173.5) * mm, "radius": 2.5 * mm});
            skCircle(sketch, "E161", {"center": v(140, 123.5) * mm, "radius": 2.5 * mm});
            skCircle(sketch, "E162", {"center": v(140, 109.5) * mm, "radius": 2.5 * mm});
            skSolve(sketch);
        }
        {
            var Q0;
            Q0=makeQuery(id+"F6.imprint","IMPRINT",FACE,{"disambiguationData":[TD([[makeQuery(id+"F6.imprint","IMPRINT",EDGE,{"derivedFrom":sQuery(id+"F6.wireOp",EDGE,"E113.top")}),-1.0]])]});
            extrude(context, id + "F7", {"entities" : qUnion([Q0]), "depth" : (getVariable(context, 'thick')) * mm});
        }
        {
            var Q0;
            Q0=qCreatedBy(makeId("Top.planeOp"),FACE);
            var sketch = newSketch(context, id + "F8", { "sketchPlane" : qUnion([Q0])});
            skLineSegment(sketch, "E163.bottom", {"start": v(240, -150) * mm, "end": v(215, -150) * mm});
            skLineSegment(sketch, "E163.top", {"start": v(240, 150) * mm, "end": v(210, 150) * mm});
            skLineSegment(sketch, "E163.left", {"start": v(240, -150) * mm, "end": v(240, -90) * mm});
            skLineSegment(sketch, "E163.right", {"start": v(-240, -150) * mm, "end": v(-240, -120) * mm});
            skPoint(sketch, "E163.middle", {"position": v(0, 0) * mm});
            skLineSegment(sketch, "E164.bottom", {"start": v(-24.5, 150) * mm, "end": v(24.5, 150) * mm});
            skLineSegment(sketch, "E164.top", {"start": v(-24.5, 107) * mm, "end": v(24.5, 107) * mm});
            skLineSegment(sketch, "E164.left", {"start": v(-24.5, 146.8) * mm, "end": v(-24.5, 107) * mm});
            skLineSegment(sketch, "E164.right", {"start": v(24.5, 146.8) * mm, "end": v(24.5, 107) * mm});
            skLineSegment(sketch, "E165", {"start": v(0, 0) * mm, "end": v(0, 107) * mm, "construction": true});
            skLineSegment(sketch, "E166", {"start": v(-24.5, 146.8) * mm, "end": v(-37.5, 146.8) * mm});
            skLineSegment(sketch, "E167", {"start": v(-37.5, 146.8) * mm, "end": v(-37.5, 150) * mm});
            skLineSegment(sketch, "E168", {"start": v(24.5, 146.8) * mm, "end": v(37.5, 146.8) * mm});
            skLineSegment(sketch, "E169", {"start": v(37.5, 146.8) * mm, "end": v(37.5, 150) * mm});
            skLineSegment(sketch, "E170.bottom", {"start": v(-240, 90) * mm, "end": v(-260, 90) * mm});
            skLineSegment(sketch, "E170.top", {"start": v(-240, -120) * mm, "end": v(-260, -120) * mm});
            skLineSegment(sketch, "E170.right", {"start": v(-260, 90) * mm, "end": v(-260, -120) * mm});
            skLineSegment(sketch, "E171.bottom", {"start": v(240, 120) * mm, "end": v(260, 120) * mm});
            skLineSegment(sketch, "E171.top", {"start": v(240, -90) * mm, "end": v(260, -90) * mm});
            skLineSegment(sketch, "E171.right", {"start": v(260, 120) * mm, "end": v(260, -90) * mm});
            skLineSegment(sketch, "E172.top", {"start": v(-215, -170) * mm, "end": v(215, -170) * mm});
            skLineSegment(sketch, "E172.left", {"start": v(-215, -150) * mm, "end": v(-215, -170) * mm});
            skLineSegment(sketch, "E172.right", {"start": v(215, -150) * mm, "end": v(215, -170) * mm});
            skArc(sketch, "E173", {"start": v(240, -125) * mm, "mid": v(222.32, -132.32) * mm, "end": v(215, -150) * mm});
            skArc(sketch, "E174", {"start": v(-240, 125) * mm, "mid": v(-222.32, 132.32) * mm, "end": v(-215, 150) * mm});
            skArc(sketch, "E175", {"start": v(215, 150) * mm, "mid": v(222.32, 132.32) * mm, "end": v(240, 125) * mm});
            skCircle(sketch, "E176", {"center": v(250, 95) * mm, "radius": 2 * mm});
            skPoint(sketch, "E176.centerSnap0", {"position": v(250, 120) * mm});
            skCircle(sketch, "E177", {"center": v(250, -65) * mm, "radius": 2 * mm});
            skCircle(sketch, "E178", {"center": v(-250, -95) * mm, "radius": 2 * mm});
            skPoint(sketch, "E178.centerSnap0", {"position": v(-250, -120) * mm});
            skCircle(sketch, "E179", {"center": v(-250, 65) * mm, "radius": 2 * mm});
            skCircle(sketch, "E180", {"center": v(-185, -160) * mm, "radius": 2 * mm});
            skPoint(sketch, "E180.centerSnap0", {"position": v(-215, -160) * mm});
            skCircle(sketch, "E181", {"center": v(175, -160) * mm, "radius": 2 * mm});
            skLineSegment(sketch, "E182", {"start": v(-210, 150) * mm, "end": v(-210, 170) * mm});
            skLineSegment(sketch, "E183", {"start": v(-210, 170) * mm, "end": v(-180, 170) * mm});
            skLineSegment(sketch, "E184", {"start": v(-180, 170) * mm, "end": v(-180, 150) * mm});
            skLineSegment(sketch, "E185", {"start": v(210, 150) * mm, "end": v(210, 170) * mm});
            skLineSegment(sketch, "E186", {"start": v(210, 170) * mm, "end": v(180, 170) * mm});
            skLineSegment(sketch, "E187", {"start": v(180, 170) * mm, "end": v(180, 150) * mm});
            skCircle(sketch, "E188", {"center": v(-195, 160) * mm, "radius": 2 * mm});
            skPoint(sketch, "E188.centerSnap0", {"position": v(-180, 160) * mm});
            skPoint(sketch, "E188.centerSnap1", {"position": v(-195, 170) * mm});
            skCircle(sketch, "E189", {"center": v(195, 160) * mm, "radius": 2 * mm});
            skPoint(sketch, "E189.centerSnap0", {"position": v(195, 170) * mm});
            skPoint(sketch, "E189.centerSnap1", {"position": v(210, 160) * mm});
            skLineSegment(sketch, "E190.trimOffspring", {"start": v(180, 150) * mm, "end": v(-180, 150) * mm});
            skLineSegment(sketch, "E191.trimOffspring", {"start": v(-210, 150) * mm, "end": v(-240, 150) * mm});
            skLineSegment(sketch, "E192.trimOffspring", {"start": v(240, 120) * mm, "end": v(240, 150) * mm});
            skLineSegment(sketch, "E193.trimOffspring", {"start": v(-240, 90) * mm, "end": v(-240, 150) * mm});
            skLineSegment(sketch, "E194.trimOffspring", {"start": v(-215, -150) * mm, "end": v(-240, -150) * mm});
            skArc(sketch, "E195", {"start": v(-240, -125) * mm, "mid": v(-222.32, -132.32) * mm, "end": v(-215, -150) * mm});
            skLineSegment(sketch, "E196.bottom", {"start": v(229, 47.5) * mm, "end": v(227, 47.5) * mm});
            skLineSegment(sketch, "E196.top", {"start": v(229, 52.5) * mm, "end": v(227, 52.5) * mm});
            skLineSegment(sketch, "E196.left", {"start": v(229, 47.5) * mm, "end": v(229, 52.5) * mm});
            skLineSegment(sketch, "E196.right", {"start": v(227, 47.5) * mm, "end": v(227, 52.5) * mm});
            skPoint(sketch, "E196.middle", {"position": v(228, 50) * mm});
            skLineSegment(sketch, "E197.bottom", {"start": v(235, 52.5) * mm, "end": v(237, 52.5) * mm});
            skLineSegment(sketch, "E197.top", {"start": v(235, 47.5) * mm, "end": v(237, 47.5) * mm});
            skLineSegment(sketch, "E197.left", {"start": v(235, 52.5) * mm, "end": v(235, 47.5) * mm});
            skLineSegment(sketch, "E197.right", {"start": v(237, 52.5) * mm, "end": v(237, 47.5) * mm});
            skPoint(sketch, "E197.middle", {"position": v(236, 50) * mm});
            skLineSegment(sketch, "E198.bottom", {"start": v(227, -47.5) * mm, "end": v(229, -47.5) * mm});
            skLineSegment(sketch, "E198.top", {"start": v(227, -52.5) * mm, "end": v(229, -52.5) * mm});
            skLineSegment(sketch, "E198.left", {"start": v(227, -47.5) * mm, "end": v(227, -52.5) * mm});
            skLineSegment(sketch, "E198.right", {"start": v(229, -47.5) * mm, "end": v(229, -52.5) * mm});
            skPoint(sketch, "E198.middle", {"position": v(228, -50) * mm});
            skLineSegment(sketch, "E199.bottom", {"start": v(235, -47.5) * mm, "end": v(237, -47.5) * mm});
            skLineSegment(sketch, "E199.top", {"start": v(235, -52.5) * mm, "end": v(237, -52.5) * mm});
            skLineSegment(sketch, "E199.left", {"start": v(235, -47.5) * mm, "end": v(235, -52.5) * mm});
            skLineSegment(sketch, "E199.right", {"start": v(237, -47.5) * mm, "end": v(237, -52.5) * mm});
            skPoint(sketch, "E199.middle", {"position": v(236, -50) * mm});
            skPoint(sketch, "E200", {"position": v(232, -50) * mm});
            skPoint(sketch, "E201", {"position": v(232, 50) * mm});
            skSolve(sketch);
        }
        {
            var Q0;
            {var subQ11=sQuery(id+"F8.wireOp",EDGE,"E164.top");Q0=makeQuery(id+"F8.imprint","IMPRINT",FACE,{"disambiguationData":[TD([[makeQuery(id+"F8.imprint","IMPRINT",EDGE,{"derivedFrom":subQ11}),-1.0]])]});}
            var Q1;
            {var subQ0=sQuery(id+"F8.wireOp",EDGE,"E182");Q1=makeQuery(id+"F8.imprint","IMPRINT",FACE,{"disambiguationData":[TD([[makeQuery(id+"F8.imprint","IMPRINT",EDGE,{"derivedFrom":subQ0}),-1.0]])]});}
            var Q2;
            {var subQ1=sQuery(id+"F8.wireOp",EDGE,"E185");Q2=makeQuery(id+"F8.imprint","IMPRINT",FACE,{"disambiguationData":[TD([[makeQuery(id+"F8.imprint","IMPRINT",EDGE,{"derivedFrom":subQ1}),1.0]])]});}
            var Q3;
            Q3=makeQuery(id+"F8.imprint","IMPRINT",FACE,{"disambiguationData":[TD([[makeQuery(id+"F8.imprint","IMPRINT",EDGE,{"derivedFrom":sQuery(id+"F8.wireOp",EDGE,"E171.bottom")}),-1.0]])]});
            var Q4;
            Q4=makeQuery(id+"F8.imprint","IMPRINT",FACE,{"disambiguationData":[TD([[makeQuery(id+"F8.imprint","IMPRINT",EDGE,{"derivedFrom":sQuery(id+"F8.wireOp",EDGE,"E170.bottom")}),1.0]])]});
            var Q5;
            Q5=makeQuery(id+"F8.imprint","IMPRINT",FACE,{"disambiguationData":[TD([[makeQuery(id+"F8.imprint","IMPRINT",EDGE,{"derivedFrom":sQuery(id+"F8.wireOp",EDGE,"E172.bottom")}),-1.0]])]});
            extrude(context, id + "F9", {"entities" : qUnion([Q0, Q1, Q2, Q3, Q4, Q5]), "depth" : (getVariable(context, 'thick')) * mm});
        }
    });
